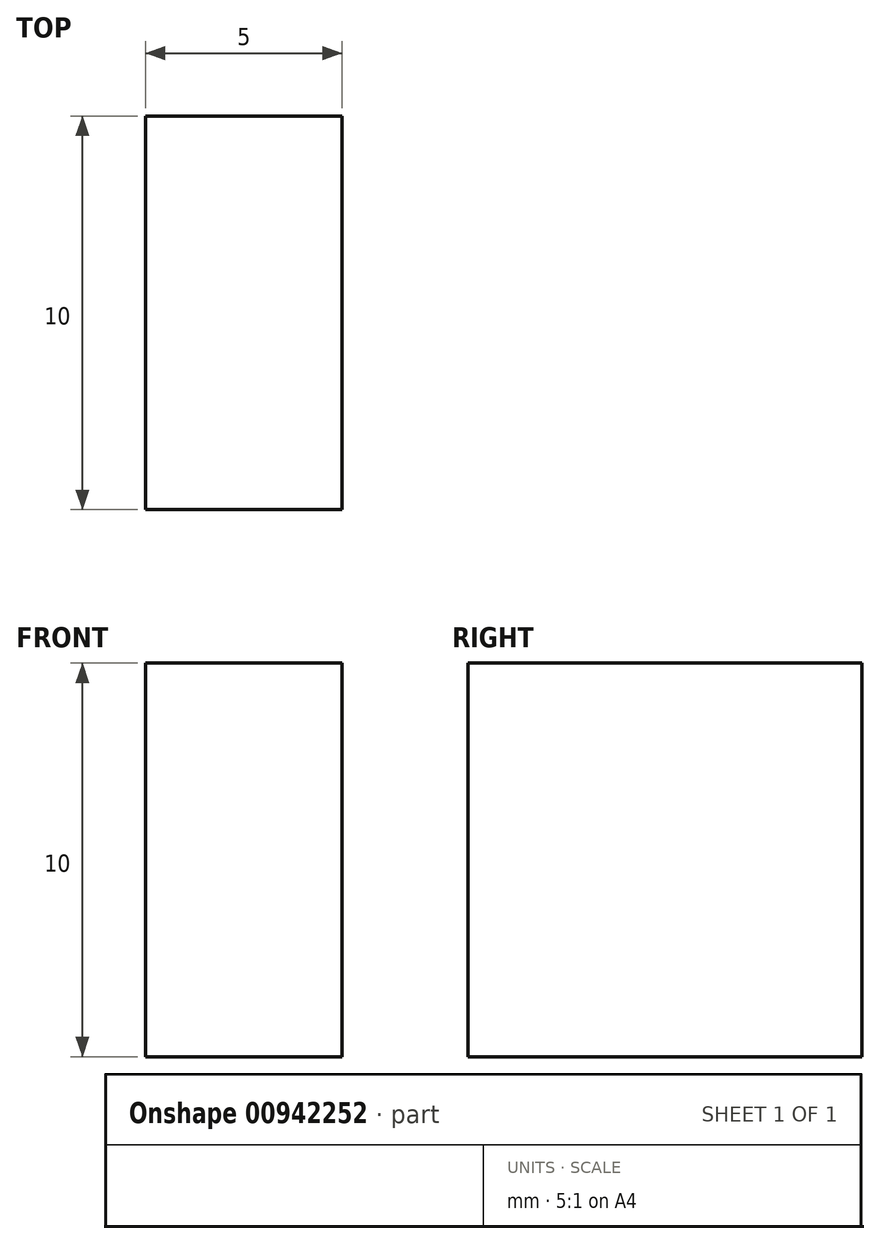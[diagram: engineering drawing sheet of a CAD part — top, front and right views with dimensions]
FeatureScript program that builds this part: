
annotation { "Feature Type Name" : "Feature", "Feature Type Description" : "" }
export const myFeature = defineFeature(function(context is Context, id is Id, definition is map)
    precondition{}
    {
        {
            var Q0;
            Q0=qCreatedBy(makeId("Top.planeOp"),FACE);
            var sketch = newSketch(context, id + "F0", { "sketchPlane" : qUnion([Q0])});
            skLineSegment(sketch, "E0.bottom", {"start": v(2.5, 5) * mm, "end": v(-2.5, 5) * mm});
            skLineSegment(sketch, "E0.top", {"start": v(2.5, -5) * mm, "end": v(-2.5, -5) * mm});
            skLineSegment(sketch, "E0.left", {"start": v(2.5, 5) * mm, "end": v(2.5, -5) * mm});
            skLineSegment(sketch, "E0.right", {"start": v(-2.5, 5) * mm, "end": v(-2.5, -5) * mm});
            skPoint(sketch, "E0.middle", {"position": v(0, 0) * mm});
            skSolve(sketch);
        }
        {
            var Q0;
            Q0 = qSketchRegion(id + "F0", true);
            extrude(context, id + "F1", {"entities" : qUnion([Q0]), "depth" : 10 * mm, "offsetDistance" : 25 * mm});
        }
    });
